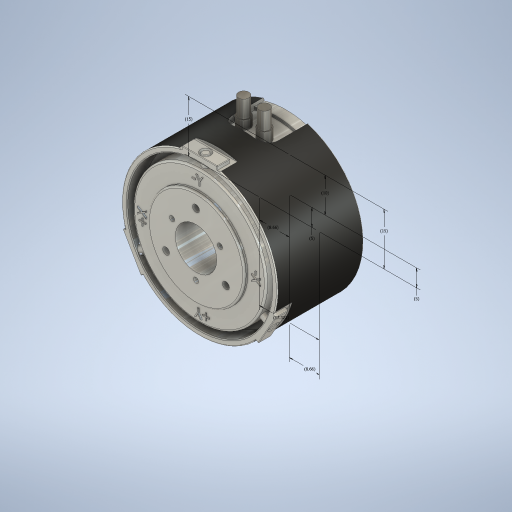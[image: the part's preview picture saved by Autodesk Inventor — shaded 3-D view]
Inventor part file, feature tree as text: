
AUTODESK INVENTOR PART (.ipt)
format: ipt  version: 2024 (Build 280153000, 153)  size: 827,392 bytes
history: native  units: mm
features: extrude x20, fillet x7, hole x4, sketch x4, plane x2, emboss x1, projected_geometry x1
ambient origin geometry x8: Origin, YZ Plane, XZ Plane, XY Plane, X Axis, Y Axis, Z Axis, Center Point
bodies: Body1 (feature_tree)
feature tree (39):
  extrude  "Extrusion2"  Depth=12.0mm
  fillet  "Fillet1"  Radius=27.0mm
  extrude  "Extrusion3"  Depth=1.5mm
  fillet  "Fillet2"  Radius=1.5mm
  extrude  "Extrusion5"  Depth=0.25mm
  extrude  "Extrusion7"  Depth=12.0mm
  extrude  "Extrusion8"  Depth=0.5mm
  extrude  "Extrusion9"  Depth=0.5mm
  extrude  "Extrusion10"  Depth=0.5mm TaperAngle=360.0deg
  extrude  "Extrusion11"  Depth=5.0mm TaperAngle=0.0deg
  extrude  "Extrusion12"  Depth=0.5mm
  extrude  "Extrusion13"  Depth=0.5mm
  extrude  "Extrusion14"  Depth=4.0mm TaperAngle=0.0deg
  fillet  "Fillet4"  Radius=3.6mm
  extrude  "Extrusion15"  Depth=0.5mm
  extrude  "Extrusion16"  Depth=6.0mm
  extrude  "Extrusion17"  Depth=1.0mm TaperAngle=0.0deg
  fillet  "Fillet5"  Radius=3.0mm
  fillet  "Fillet6"  Radius=2.5mm
  hole  "Hole1"  [1 undecoded]
  hole  "Hole2"  [1 undecoded]
  plane  "Work Plane1"
  emboss  "Emboss1"
  extrude  "Extrusion18"  Depth=0.5mm
  fillet  "Fillet7"  Radius=1.4mm
  plane  "Work Plane2"
  extrude  "Extrusion19"  Depth=0.5mm
  extrude  "Extrusion20"  Depth=1.0mm TaperAngle=0.0deg
  extrude  "Extrusion21"  Depth=0.5mm
  extrude  "Extrusion22"  Depth=0.5mm
  sketch  "Sketch28"  dims[d11=25.0mm d12=0.0mm d15=0.25mm]
  fillet  "Fillet8"  Radius=3.0mm
  extrude  "Extrusion23"  Depth=0.5mm
  hole  "Hole3"  [1 undecoded]
  hole  "Hole4"  [1 undecoded]
  sketch  "Sketch31"  dims[d16=15.0mm d17=0.0mm d27=12.0mm d28=1.75mm d29=22.5mm d30=30.0mm d32=360.0deg d34=5.0mm d35=0.0mm d36=38.5mm d37=28.0mm d38=4.0mm d39=0.0mm d41=3.6mm d42=1.4mm d43=6.0mm d44=1.0mm d45=0.0mm d46=3.0mm d47=2.5mm d48=0.0mm d49=10.333074mm d50=6.0mm d51=3.6mm d52=1.4mm d53=10.333mm d54=1.0mm d55=0.0mm d56=5.166537mm d57=1.8mm d58=3.0mm d59=1.8mm d60=5.1665mm d61=2.0mm d62=0.0mm d63=3.6mm d64=10.333mm d65=6.0mm d66=1.4mm d67=1.0mm d68=0.0mm d69=3.0mm d70=1.8mm d71=5.167mm d72=2.0mm d73=0.0mm d74=0.15mm d75=2.0mm d76=2.0mm d77=0.0mm d78=2.0mm d79=10.0mm d80=0.0mm d81=2.0mm d82=10.0mm d83=0.0mm d84=0.15mm d85=0.5mm d86=2.5mm d87=10.0mm d88=30.0mm d90=360.0deg d92=2.013mm d93=5.0mm d94=6.92mm d95=3.0mm d96=90.0deg d97=8.0mm d98=20.594885mm d99=1.5mm d100=8.0mm d101=30.0mm d103=360.0deg d105=1.5mm d106=6.0mm d107=4.0mm d108=2.0mm d109=90.0deg d110=5.0mm d111=0.0mm d112=5.0mm d113=4.0mm d114=3.0mm d115=2.5mm d116=15.0mm d117=3.0mm d118=4.0mm d119=15.0mm d120=2.5mm d123=3.0mm d124=4.0mm d125=15.0mm d126=3.0mm d127=4.0mm d128=3.0mm d129=15.0mm d130=3.0mm d131=0.25mm d132=0.0mm d135=1.5mm d136=1.5mm d137=12.5mm d138=6.25mm d139=12.2mm d140=0.0mm d141=3.5mm d142=23.5mm d143=3.6mm d144=3.6mm d145=6.0mm d146=3.0mm d147=3.0mm d148=3.0mm d149=12.2mm d150=0.0mm d151=3.0mm d152=3.0mm d153=5.0mm d154=0.0mm d155=2.0mm d156=0.0mm d157=43.5mm d158=42.0mm d159=10.0mm d160=0.0mm d161=0.25mm d162=10.0mm d163=0.0mm d165=2.5mm d166=10.0mm d167=30.0mm d169=360.0deg d171=2.013mm d172=5.0mm d173=4.0mm d174=2.0mm d175=90.0deg d176=8.0mm d177=20.594885mm d178=1.5mm d179=8.0mm d180=30.0mm d182=360.0deg d184=1.5mm d185=6.0mm d186=4.0mm d187=2.0mm d188=90.0deg d189=5.0mm d190=0.0mm d191=15.0mm d192=15.0mm d193=17.320508mm d194=10.0mm d195=8.660254mm d196=5.0mm d197=8.660254mm d198=5.0mm d18=0.5mm d19=0.872665mm]
  projected_geometry  "Projected Loop2"
  sketch  "Sketch21"  dims[d4=28.0mm d5=12.0mm d6=27.0mm d7=0.0mm]
  sketch  "Sketch26"  dims[d8=0.5mm d9=45.0mm d10=1.5mm]
note: 4 required parameter values undecoded (feature->parameter linkage not recoverable at this tier; creation-order binding heuristic only, values carry confidence <= 0.55)
